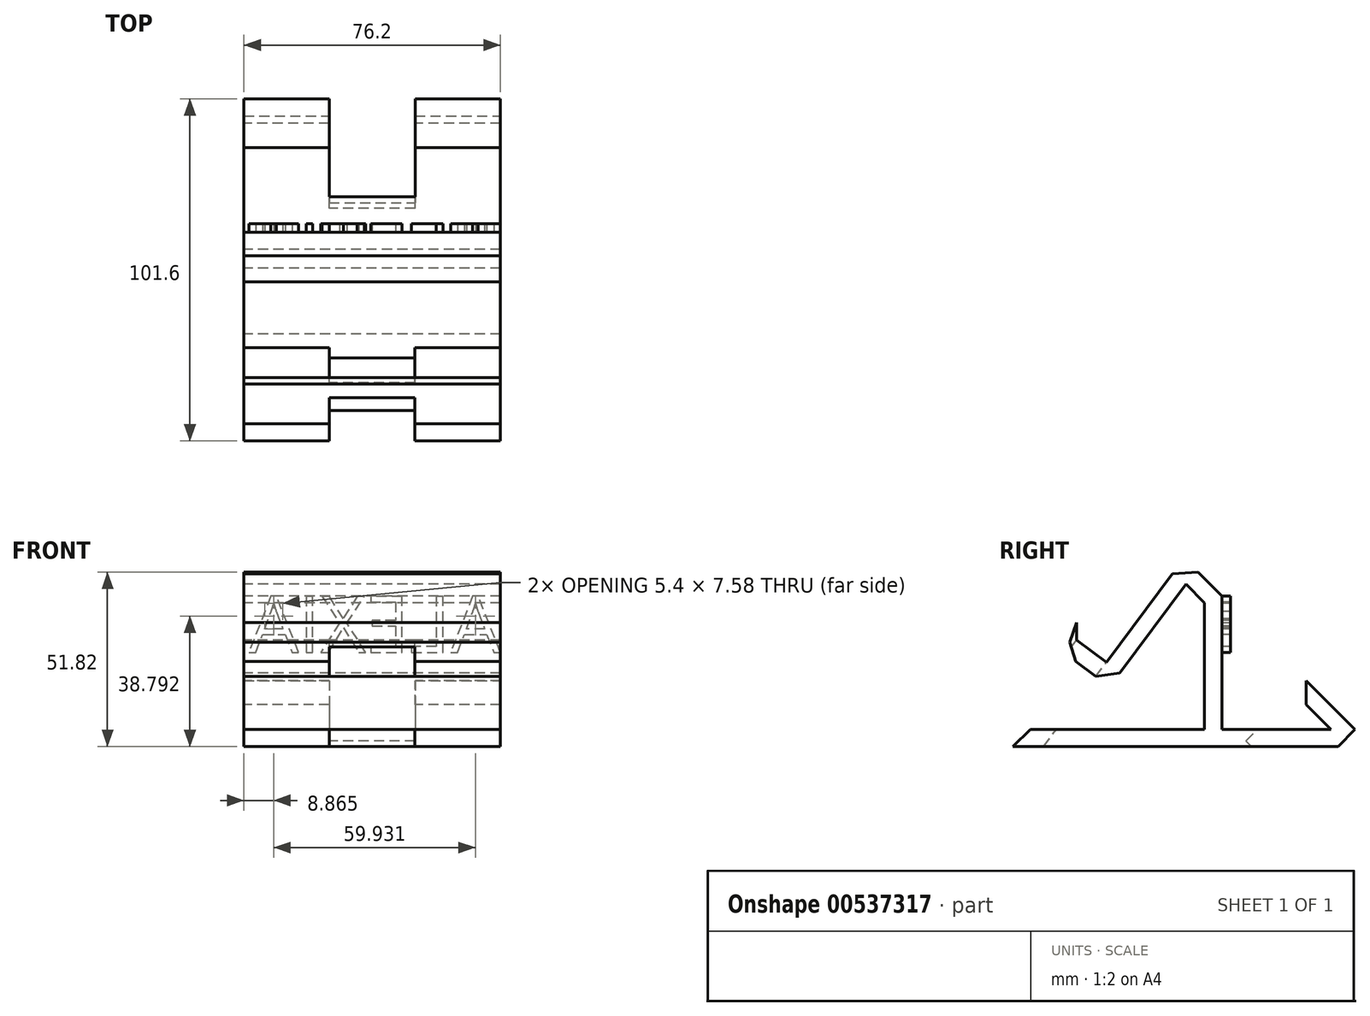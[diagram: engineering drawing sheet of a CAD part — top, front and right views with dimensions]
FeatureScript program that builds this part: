
annotation { "Feature Type Name" : "Feature", "Feature Type Description" : "" }
export const myFeature = defineFeature(function(context is Context, id is Id, definition is map)
    precondition{}
    {
        {
            var Q0;
            Q0=qCreatedBy(makeId("Right.planeOp"),FACE);
            var sketch = newSketch(context, id + "F0", { "sketchPlane" : qUnion([Q0])});
            skLineSegment(sketch, "E0", {"start": v(0, 0) * mm, "end": v(-50.8, 0) * mm});
            skLineSegment(sketch, "E1", {"start": v(0, 0) * mm, "end": v(50.8, 0) * mm});
            skLineSegment(sketch, "E2", {"start": v(-50.8, 0) * mm, "end": v(-50.8, 5.08) * mm});
            skLineSegment(sketch, "E3", {"start": v(50.8, 5.08) * mm, "end": v(50.8, 0) * mm});
            skLineSegment(sketch, "E4", {"start": v(-22.11, 17.8) * mm, "end": v(-35.1, 27.49) * mm});
            skLineSegment(sketch, "E5", {"start": v(-31.97, 31.68) * mm, "end": v(-31.97, 36.79) * mm});
            skLineSegment(sketch, "E6", {"start": v(-31.97, 36.79) * mm, "end": v(-35.1, 27.49) * mm});
            skLineSegment(sketch, "E7", {"start": v(11.19, 37.58) * mm, "end": v(11.19, 44.77) * mm});
            skLineSegment(sketch, "E8", {"start": v(11.19, 44.77) * mm, "end": v(11.19, 5.08) * mm});
            skLineSegment(sketch, "E9", {"start": v(32.7, 16) * mm, "end": v(36.3, 19.6) * mm});
            skLineSegment(sketch, "E10", {"start": v(6.07, 5.08) * mm, "end": v(6.07, 42.7) * mm});
            skLineSegment(sketch, "E11", {"start": v(11.19, 37.58) * mm, "end": v(11.19, 5.08) * mm});
            skLineSegment(sketch, "E12", {"start": v(6.07, 42.7) * mm, "end": v(0.57, 48.22) * mm});
            skLineSegment(sketch, "E13", {"start": v(0, 55.98) * mm, "end": v(11.19, 44.77) * mm});
            skLineSegment(sketch, "E14", {"start": v(32.7, 16) * mm, "end": v(43.6, 5.08) * mm});
            skLineSegment(sketch, "E15", {"start": v(36.3, 19.6) * mm, "end": v(50.8, 5.08) * mm});
            skLineSegment(sketch, "E16", {"start": v(-23.07, 25.05) * mm, "end": v(0, 55.98) * mm});
            skLineSegment(sketch, "E17", {"start": v(0.57, 48.22) * mm, "end": v(-22.11, 17.8) * mm});
            skLineSegment(sketch, "E18", {"start": v(-31.97, 31.68) * mm, "end": v(-23.07, 25.05) * mm});
            skLineSegment(sketch, "E19", {"start": v(-50.8, 5.08) * mm, "end": v(6.07, 5.08) * mm});
            skLineSegment(sketch, "E20", {"start": v(11.19, 5.08) * mm, "end": v(43.6, 5.08) * mm});
            skSolve(sketch);
        }
        {
            var Q0;
            Q0=makeQuery(id+"F0.imprint","IMPRINT",FACE,{"disambiguationData":[TD([[makeQuery(id+"F0.imprint","IMPRINT",EDGE,{"derivedFrom":sQuery(id+"F0.wireOp",EDGE,"E0")}),-1.0]])]});
            extrude(context, id + "F1", {"entities" : qUnion([Q0]), "depth" : 38.1 * mm, "offsetDistance" : 25.4 * mm, "hasSecondDirection" : true, "secondDirectionOppositeDirection" : true, "secondDirectionDepth" : 38.1 * mm});
        }
        {
            var Q0;
            Q0=makeQuery(id+"F1.opExtrude","SWEPT_FACE",FACE,{"disambiguationData":[OSD([sQuery(id+"F0.wireOp",EDGE,"E18")])]});
            var sketch = newSketch(context, id + "F2", { "sketchPlane" : qUnion([Q0])});
            skLineSegment(sketch, "E21.bottom", {"start": v(12.71, -33.47) * mm, "end": v(-12.71, -33.47) * mm});
            skLineSegment(sketch, "E21.top", {"start": v(12.71, -44.57) * mm, "end": v(-12.71, -44.57) * mm});
            skLineSegment(sketch, "E21.left", {"start": v(12.71, -33.47) * mm, "end": v(12.71, -44.57) * mm});
            skLineSegment(sketch, "E21.right", {"start": v(-12.71, -33.47) * mm, "end": v(-12.71, -44.57) * mm});
            skSolve(sketch);
        }
        {
            var Q0;
            Q0=makeQuery(id+"F2.imprint","IMPRINT",FACE,{"disambiguationData":[TD([[makeQuery(id+"F2.imprint","IMPRINT",EDGE,{"derivedFrom":sQuery(id+"F2.wireOp",EDGE,"E21.bottom")}),1.0]])]});
            extrude(context, id + "F3", {"entities" : qUnion([Q0]), "operationType" : NewBodyOperationType.REMOVE, "oppositeDirection" : true, "depth" : 50.8 * mm, "offsetDistance" : 25.4 * mm});
        }
        {
            var Q0;
            Q0=makeQuery(id+"F1.opExtrude","SWEPT_FACE",FACE,{"disambiguationData":[OSD([sQuery(id+"F0.wireOp",EDGE,"E15")])]});
            var sketch = newSketch(context, id + "F4", { "sketchPlane" : qUnion([Q0])});
            skLineSegment(sketch, "E22.bottom", {"start": v(12.76, -11.77) * mm, "end": v(-12.76, -11.77) * mm});
            skLineSegment(sketch, "E22.top", {"start": v(12.76, -42.55) * mm, "end": v(-12.76, -42.55) * mm});
            skLineSegment(sketch, "E22.left", {"start": v(12.76, -11.77) * mm, "end": v(12.76, -42.55) * mm});
            skLineSegment(sketch, "E22.right", {"start": v(-12.76, -11.77) * mm, "end": v(-12.76, -42.55) * mm});
            skLineSegment(sketch, "E23", {"start": v(12.76, -32.29) * mm, "end": v(38.1, -32.29) * mm});
            skLineSegment(sketch, "E24", {"start": v(-12.76, -32.29) * mm, "end": v(-38.1, -32.29) * mm});
            skSolve(sketch);
        }
        {
            var Q0;
            {var subQ0=sQuery(id+"F4.wireOp",EDGE,"E22.bottom");Q0=makeQuery(id+"F4.imprint","IMPRINT",FACE,{"disambiguationData":[TD([[makeQuery(id+"F4.imprint","IMPRINT",EDGE,{"derivedFrom":subQ0}),-1.0]])]});}
            var Q1;
            {var subQ0=sQuery(id+"F4.wireOp",EDGE,"E22.top");Q1=makeQuery(id+"F4.imprint","IMPRINT",FACE,{"disambiguationData":[TD([[makeQuery(id+"F4.imprint","IMPRINT",EDGE,{"derivedFrom":subQ0}),-1.0]])]});}
            extrude(context, id + "F5", {"entities" : qUnion([Q0, Q1]), "operationType" : NewBodyOperationType.REMOVE, "oppositeDirection" : true, "depth" : 25.4 * mm, "offsetDistance" : 25.4 * mm});
        }
        {
            var Q0;
            Q0=makeQuery(id+"F1.opExtrude","SWEPT_FACE",FACE,{"disambiguationData":[OSD([sQuery(id+"F0.wireOp",EDGE,"E8"),sQuery(id+"F0.wireOp",EDGE,"E11")])]});
            var sketch = newSketch(context, id + "F6", { "sketchPlane" : qUnion([Q0])});
            skText(sketch, "E25", { "text": "ALEXIA", "fontName": "OpenSans-Regular.ttf"});
            const initialGuessF6  = {"E25": [-0.0381, 0.02795, 1, 0, 0.01683]};
            skSetInitialGuess(sketch, initialGuessF6);
            skSolve(sketch);
        }
        {
            var Q0;
            Q0=makeQuery(id+"F6.imprint","IMPRINT",FACE,{"disambiguationData":[TD([[makeQuery(id+"F6.imprint","IMPRINT",EDGE,{"derivedFrom":sQuery(id+"F6.wireOp",EDGE,"E25.sketch_text.stroke-0")}),-1.0]])]});
            var Q1;
            Q1=makeQuery(id+"F6.imprint","IMPRINT",FACE,{"disambiguationData":[TD([[makeQuery(id+"F6.imprint","IMPRINT",EDGE,{"derivedFrom":sQuery(id+"F6.wireOp",EDGE,"E25.sketch_text.stroke-13")}),-1.0]])]});
            var Q2;
            Q2=makeQuery(id+"F6.imprint","IMPRINT",FACE,{"disambiguationData":[TD([[makeQuery(id+"F6.imprint","IMPRINT",EDGE,{"derivedFrom":sQuery(id+"F6.wireOp",EDGE,"E25.sketch_text.stroke-19")}),-1.0]])]});
            var Q3;
            Q3=makeQuery(id+"F6.imprint","IMPRINT",FACE,{"disambiguationData":[TD([[makeQuery(id+"F6.imprint","IMPRINT",EDGE,{"derivedFrom":sQuery(id+"F6.wireOp",EDGE,"E25.sketch_text.stroke-31")}),-1.0]])]});
            var Q4;
            Q4=makeQuery(id+"F6.imprint","IMPRINT",FACE,{"disambiguationData":[TD([[makeQuery(id+"F6.imprint","IMPRINT",EDGE,{"derivedFrom":sQuery(id+"F6.wireOp",EDGE,"E25.sketch_text.stroke-43")}),-1.0]])]});
            var Q5;
            Q5=makeQuery(id+"F6.imprint","IMPRINT",FACE,{"disambiguationData":[TD([[makeQuery(id+"F6.imprint","IMPRINT",EDGE,{"derivedFrom":sQuery(id+"F6.wireOp",EDGE,"E25.sketch_text.stroke-47")}),-1.0]])]});
            extrude(context, id + "F7", {"entities" : qUnion([Q0, Q1, Q2, Q3, Q4, Q5]), "depth" : 2.54 * mm, "offsetDistance" : 25.4 * mm});
        }
        {
            var Q0;
            Q0=makeQuery(id+"F1.opExtrude","SWEPT_EDGE",EDGE,{"disambiguationData":[OSD([sQuery(id+"F0.wireOp",EDGE,"E13"),sQuery(id+"F0.wireOp",EDGE,"E16")])]});
            var Q1;
            Q1=makeQuery(id+"F1.opExtrude","SWEPT_EDGE",EDGE,{"disambiguationData":[OSD([sQuery(id+"F0.wireOp",EDGE,"E4"),sQuery(id+"F0.wireOp",EDGE,"E17")])]});
            var Q2;
            {var subQ0=sQuery(id+"F0.wireOp",EDGE,"E4");var subQ1=makeQuery(id+"F1.opExtrude","SWEPT_FACE",FACE,{"disambiguationData":[OSD([subQ0])]});var subQ2=sQuery(id+"F0.wireOp",EDGE,"E6");var subQ3=makeQuery(id+"F1.opExtrude","SWEPT_FACE",FACE,{"disambiguationData":[OSD([subQ2])]});Q2=makeQuery(id+"F3.boolean.opBoolean","SPLIT",EDGE,{"disambiguationData":[topologyDisambiguationEdgeConnected([subQ1,subQ3]),TD([makeQuery(id+"F3.opExtrude","SWEPT_FACE",FACE,{"disambiguationData":[OSD([sQuery(id+"F2.wireOp",EDGE,"E21.left")])]})])],"derivedFrom":makeQuery(id+"F1.opExtrude","SWEPT_EDGE",EDGE,{"disambiguationData":[OSD([subQ0,subQ2])]})});}
            var Q3;
            {var subQ0=sQuery(id+"F0.wireOp",EDGE,"E1");var subQ2=sQuery(id+"F0.wireOp",EDGE,"E3");Q3=makeQuery(id+"F5.boolean.opBoolean","SPLIT",EDGE,{"disambiguationData":[TD([makeQuery(id+"F5.opExtrude","SWEPT_FACE",FACE,{"disambiguationData":[OSD([sQuery(id+"F4.wireOp",EDGE,"E22.right")])]})])],"derivedFrom":makeQuery(id+"F1.opExtrude","SWEPT_EDGE",EDGE,{"disambiguationData":[OSD([subQ0,subQ2])]})});}
            var Q4;
            {var subQ0=sQuery(id+"F0.wireOp",EDGE,"E1");var subQ2=sQuery(id+"F0.wireOp",EDGE,"E3");Q4=makeQuery(id+"F5.boolean.opBoolean","SPLIT",EDGE,{"disambiguationData":[TD([makeQuery(id+"F5.opExtrude","SWEPT_FACE",FACE,{"disambiguationData":[OSD([sQuery(id+"F4.wireOp",EDGE,"E22.left")])]})])],"derivedFrom":makeQuery(id+"F1.opExtrude","SWEPT_EDGE",EDGE,{"disambiguationData":[OSD([subQ0,subQ2])]})});}
            var Q5;
            {var subQ0=sQuery(id+"F0.wireOp",EDGE,"E14");var subQ1=sQuery(id+"F0.wireOp",EDGE,"E9");Q5=makeQuery(id+"F5.boolean.opBoolean","SPLIT",EDGE,{"disambiguationData":[TD([makeQuery(id+"F5.opExtrude","SWEPT_FACE",FACE,{"disambiguationData":[OSD([sQuery(id+"F4.wireOp",EDGE,"E22.left")])]})])],"derivedFrom":makeQuery(id+"F1.opExtrude","SWEPT_EDGE",EDGE,{"disambiguationData":[OSD([subQ1,subQ0])]})});}
            var Q6;
            {var subQ0=sQuery(id+"F0.wireOp",EDGE,"E14");var subQ1=sQuery(id+"F0.wireOp",EDGE,"E9");Q6=makeQuery(id+"F5.boolean.opBoolean","SPLIT",EDGE,{"disambiguationData":[TD([makeQuery(id+"F5.opExtrude","SWEPT_FACE",FACE,{"disambiguationData":[OSD([sQuery(id+"F4.wireOp",EDGE,"E22.right")])]})])],"derivedFrom":makeQuery(id+"F1.opExtrude","SWEPT_EDGE",EDGE,{"disambiguationData":[OSD([subQ1,subQ0])]})});}
            var Q7;
            {var subQ0=sQuery(id+"F0.wireOp",EDGE,"E19");var subQ1=sQuery(id+"F0.wireOp",EDGE,"E2");Q7=makeQuery(id+"F3.boolean.opBoolean","SPLIT",EDGE,{"disambiguationData":[TD([makeQuery(id+"F3.opExtrude","SWEPT_FACE",FACE,{"disambiguationData":[OSD([sQuery(id+"F2.wireOp",EDGE,"E21.left")])]})])],"derivedFrom":makeQuery(id+"F1.opExtrude","SWEPT_EDGE",EDGE,{"disambiguationData":[OSD([subQ1,subQ0])]})});}
            var Q8;
            {var subQ0=sQuery(id+"F0.wireOp",EDGE,"E19");var subQ1=sQuery(id+"F0.wireOp",EDGE,"E2");Q8=makeQuery(id+"F3.boolean.opBoolean","SPLIT",EDGE,{"disambiguationData":[TD([makeQuery(id+"F3.opExtrude","SWEPT_FACE",FACE,{"disambiguationData":[OSD([sQuery(id+"F2.wireOp",EDGE,"E21.right")])]})])],"derivedFrom":makeQuery(id+"F1.opExtrude","SWEPT_EDGE",EDGE,{"disambiguationData":[OSD([subQ1,subQ0])]})});}
            chamfer(context, id + "F8", {"entities" : qUnion([Q0, Q1, Q2, Q3, Q4, Q5, Q6, Q7, Q8]), "width" : 5.08 * mm, "tangentPropagation" : true});
        }
    });
